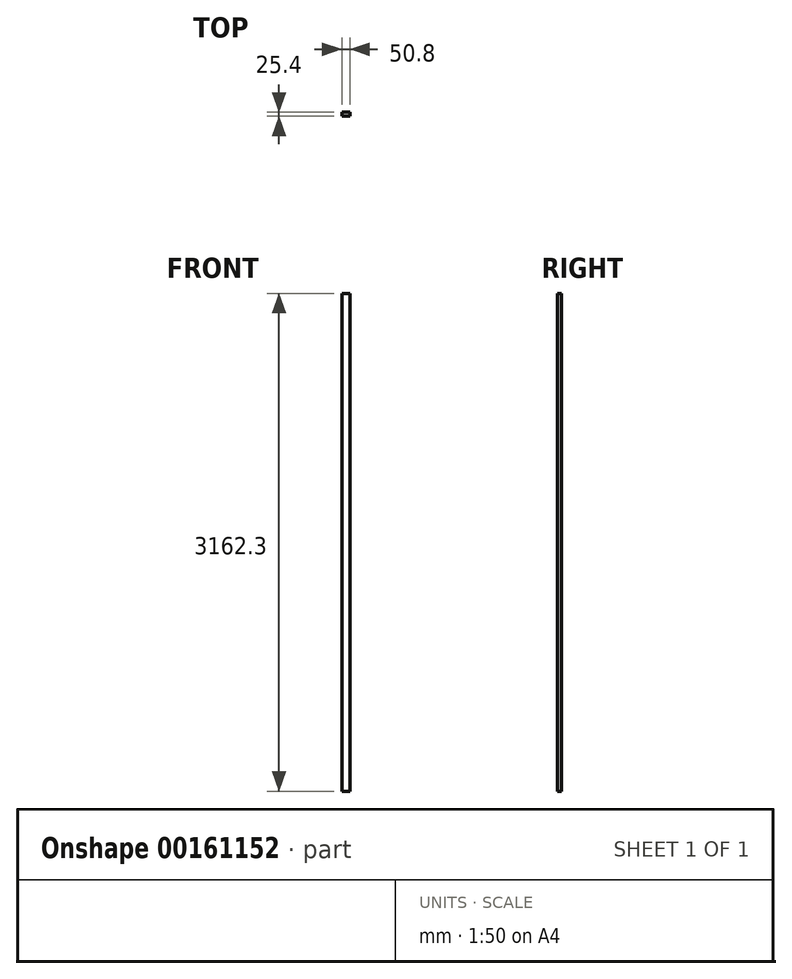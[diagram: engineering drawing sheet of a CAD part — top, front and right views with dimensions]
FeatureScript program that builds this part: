
annotation { "Feature Type Name" : "Feature", "Feature Type Description" : "" }
export const myFeature = defineFeature(function(context is Context, id is Id, definition is map)
    precondition{}
    {
        {
            var Q0;
            Q0=qCreatedBy(makeId("Top.planeOp"),FACE);
            var sketch = newSketch(context, id + "F0", { "sketchPlane" : qUnion([Q0])});
            skLineSegment(sketch, "E0.bottom", {"start": v(0, 0) * mm, "end": v(50.8, 0) * mm});
            skLineSegment(sketch, "E0.top", {"start": v(0, 25.4) * mm, "end": v(50.8, 25.4) * mm});
            skLineSegment(sketch, "E0.left", {"start": v(0, 0) * mm, "end": v(0, 25.4) * mm});
            skLineSegment(sketch, "E0.right", {"start": v(50.8, 0) * mm, "end": v(50.8, 25.4) * mm});
            skSolve(sketch);
        }
        {
            var Q0;
            Q0=qSketchRegion(id+"F0",true);
            extrude(context, id + "F1", {"entities" : qUnion([Q0]), "depth" : 3162.3 * mm});
        }
    });
